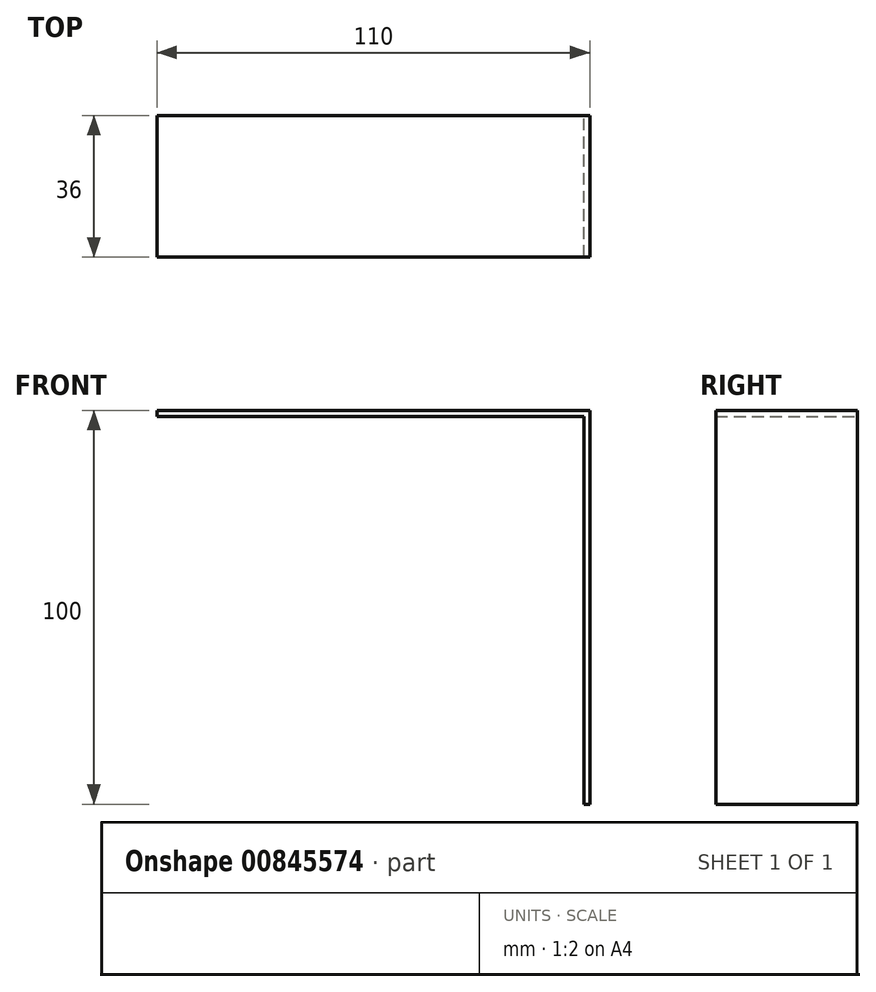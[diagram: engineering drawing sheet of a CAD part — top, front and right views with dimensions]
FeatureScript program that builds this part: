
annotation { "Feature Type Name" : "Feature", "Feature Type Description" : "" }
export const myFeature = defineFeature(function(context is Context, id is Id, definition is map)
    precondition{}
    {
        {
            var Q0;
            Q0=qCreatedBy(makeId("Front.planeOp"),FACE);
            var sketch = newSketch(context, id + "F0", { "sketchPlane" : qUnion([Q0])});
            skLineSegment(sketch, "E0", {"start": v(-59.83, 42.67) * mm, "end": v(50.17, 42.67) * mm});
            skLineSegment(sketch, "E1", {"start": v(50.17, 42.67) * mm, "end": v(50.17, -57.33) * mm});
            skLineSegment(sketch, "E2", {"start": v(48.67, -57.33) * mm, "end": v(48.67, 41.17) * mm});
            skLineSegment(sketch, "E3", {"start": v(48.67, 41.17) * mm, "end": v(-59.83, 41.17) * mm});
            skLineSegment(sketch, "E4", {"start": v(-59.83, 41.17) * mm, "end": v(-59.83, 42.67) * mm});
            skLineSegment(sketch, "E5.bottom", {"start": v(48.67, 41.17) * mm, "end": v(18.67, 41.17) * mm});
            skLineSegment(sketch, "E5.left", {"start": v(48.67, 41.17) * mm, "end": v(48.67, 8.67) * mm});
            skLineSegment(sketch, "E6", {"start": v(48.67, -57.33) * mm, "end": v(50.17, -57.33) * mm});
            skSolve(sketch);
        }
        {
            var Q0;
            Q0=makeQuery(id+"F0.imprint","IMPRINT",FACE,{"disambiguationData":[TD([[makeQuery(id+"F0.imprint","IMPRINT",EDGE,{"derivedFrom":sQuery(id+"F0.wireOp",EDGE,"E0")}),-1.0]])]});
            extrude(context, id + "F1", {"entities" : qUnion([Q0]), "depth" : 36 * mm, "offsetDistance" : 25 * mm});
        }
    });
